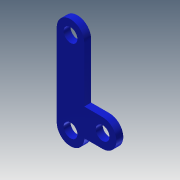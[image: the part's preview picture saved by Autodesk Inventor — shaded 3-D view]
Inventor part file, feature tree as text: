
AUTODESK INVENTOR PART (.ipt)
format: ipt  version: 2013 (Build 170138000, 138)  size: 168,960 bytes
history: native  units: mm
features: extrude x9, sketch x9
ambient origin geometry x8: Origin, YZ Plane, XZ Plane, XY Plane, X Axis, Y Axis, Z Axis, Center Point
bodies: Solid1 (feature_tree)
feature tree (18):
  extrude  "Extrusion1"  Depth=18.0mm
  extrude  "Extrusion2"  Depth=6.0mm
  extrude  "Extrusion3"  Depth=4.0mm
  extrude  "Extrusion4"  Depth=3.0mm
  extrude  "Extrusion5"  Depth=1.5mm TaperAngle=0.0deg
  extrude  "Extrusion6"  Depth=3.0mm
  extrude  "Extrusion7"  Depth=6.0mm
  extrude  "Extrusion8"  Depth=4.0mm
  extrude  "Extrusion9"  Depth=4.0mm
  sketch  "Sketch1"  dims[d0=6.0mm d1=18.0mm]
  sketch  "Sketch2"  dims[d2=6.0mm d4=6.0mm]
  sketch  "Sketch3"  dims[d5=4.0mm d6=4.0mm]
  sketch  "Sketch4"  dims[d7=2.0mm d10=3.0mm]
  sketch  "Sketch5"  dims[d11=6.0mm d12=1.5mm d13=0.0mm]
  sketch  "Sketch6"  dims[d14=3.0mm d15=3.0mm]
  sketch  "Sketch7"  dims[d16=4.0mm d17=6.0mm]
  sketch  "Sketch8"  dims[d18=1.5mm d19=0.0mm d20=4.0mm]
  sketch  "Sketch9"  dims[d21=6.0mm d22=4.0mm d23=1.5mm d24=0.0mm d25=3.0mm d26=1.5mm d27=0.0mm d28=0.2mm d29=0.2mm d30=0.2mm d31=1.5mm d32=0.0mm d33=3.0mm d34=3.0mm d35=3.0mm d36=2.0mm d37=0.0mm d38=4.0mm d39=3.0mm d40=2.0mm d41=0.0mm d42=2.0mm d43=0.0mm d44=0.5mm d45=0.0mm]
